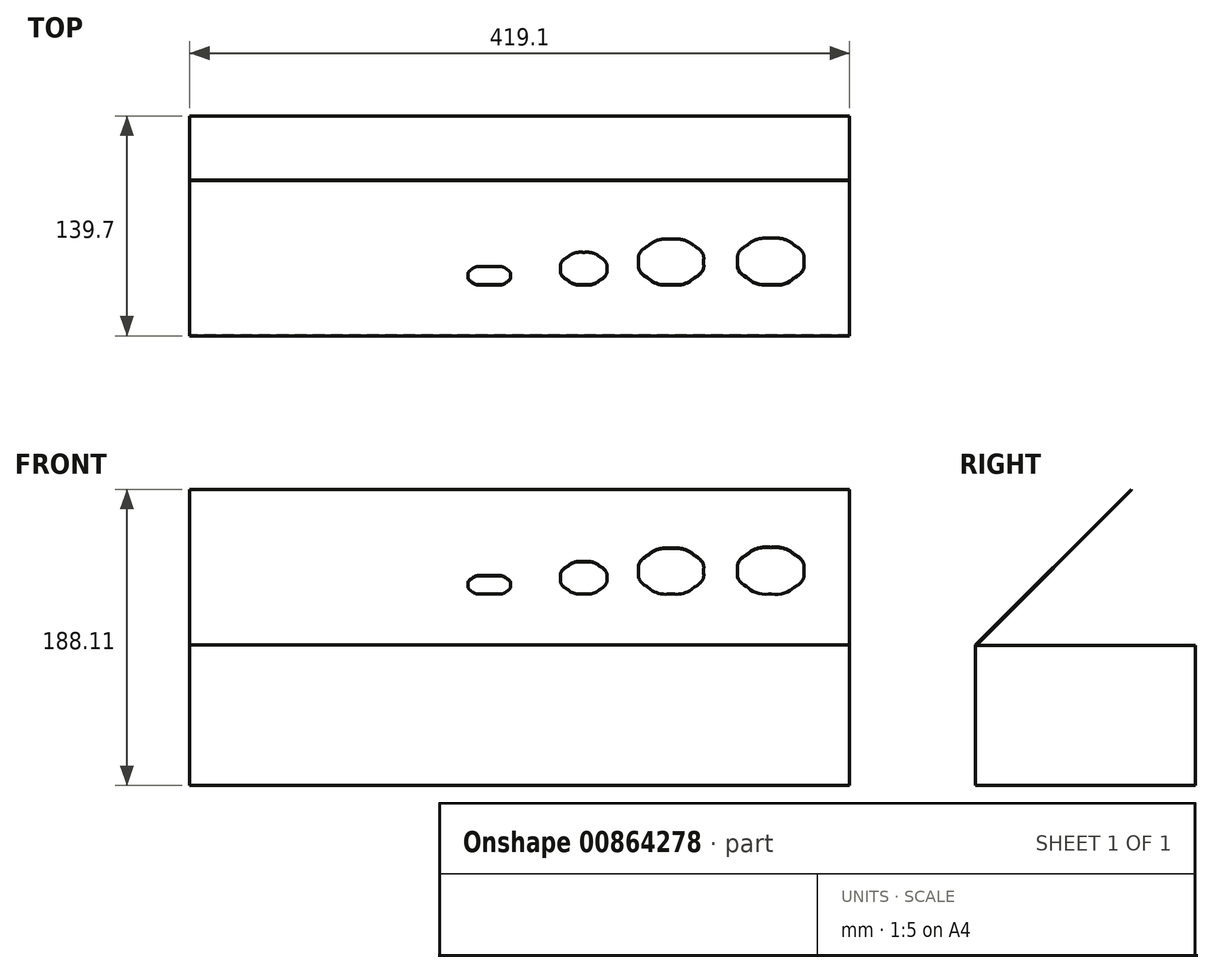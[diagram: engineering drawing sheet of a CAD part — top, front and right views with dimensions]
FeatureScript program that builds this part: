
annotation { "Feature Type Name" : "Feature", "Feature Type Description" : "" }
export const myFeature = defineFeature(function(context is Context, id is Id, definition is map)
    precondition{}
    {
        {
            var Q0;
            Q0=qCreatedBy(makeId("Right.planeOp"),FACE);
            var sketch = newSketch(context, id + "F0", { "sketchPlane" : qUnion([Q0])});
            skLineSegment(sketch, "E0.bottom", {"start": v(0, 0) * mm, "end": v(-139.7, 0) * mm});
            skLineSegment(sketch, "E0.top", {"start": v(0, 88.9) * mm, "end": v(-139.3, 88.9) * mm});
            skLineSegment(sketch, "E0.left", {"start": v(0, 0) * mm, "end": v(0, 88.9) * mm});
            skLineSegment(sketch, "E0.right", {"start": v(-139.7, 0) * mm, "end": v(-139.7, 89.32) * mm});
            skLineSegment(sketch, "E1", {"start": v(-139.7, 89.32) * mm, "end": v(-40.92, 188.1) * mm});
            skLineSegment(sketch, "E2", {"start": v(-40.92, 188.1) * mm, "end": v(-40.63, 187.82) * mm});
            skLineSegment(sketch, "E3", {"start": v(-40.63, 187.82) * mm, "end": v(-139.3, 89.15) * mm});
            skLineSegment(sketch, "E4", {"start": v(-139.3, 88.9) * mm, "end": v(-139.3, 89.15) * mm});
            skLineSegment(sketch, "E5", {"start": v(-139.3, 88.9) * mm, "end": v(-139.7, 88.9) * mm, "construction": true});
            skSolve(sketch);
        }
        {
            var Q0;
            Q0=qSketchRegion(id+"F0",true);
            extrude(context, id + "F1", {"entities" : qUnion([Q0]), "endBound" : BoundingType.SYMMETRIC, "depth" : 419.1 * mm, "offsetDistance" : 25.4 * mm});
        }
        {
            var Q0;
            Q0=makeQuery(id+"F1.opExtrude","SWEPT_FACE",FACE,{"disambiguationData":[OSD([sQuery(id+"F0.wireOp",EDGE,"E1")])]});
            var sketch = newSketch(context, id + "F2", { "sketchPlane" : qUnion([Q0])});
            skLineSegment(sketch, "E6", {"start": v(-24.54, 10.03) * mm, "end": v(-14.22, 10.03) * mm});
            skLineSegment(sketch, "E7", {"start": v(-24.54, 26.7) * mm, "end": v(-14.22, 26.7) * mm});
            skLineSegment(sketch, "E8", {"start": v(-209.88, -34.42) * mm, "end": v(-209.88, 104.5) * mm, "construction": true});
            skLineSegment(sketch, "E9", {"start": v(209.22, -34.42) * mm, "end": v(209.22, 104.5) * mm, "construction": true});
            skLineSegment(sketch, "E10", {"start": v(209.22, -34.42) * mm, "end": v(-209.88, -34.42) * mm, "construction": true});
            skLineSegment(sketch, "E11", {"start": v(-209.88, 104.5) * mm, "end": v(209.22, 104.5) * mm, "construction": true});
            skFitSpline(sketch, "E12", {"points": [v(-24.54, 26.7) * mm, v(-26.72, 26.7) * mm, v(-28.9, 25.8) * mm, v(-30.43, 24.26) * mm]});
            skFitSpline(sketch, "E13", {"points": [v(-30.43, 24.26) * mm, v(-31.98, 22.72) * mm, v(-32.88, 20.55) * mm, v(-32.88, 18.37) * mm, v(-32.88, 16.19) * mm, v(-31.98, 14.02) * mm, v(-30.43, 12.48) * mm]});
            skFitSpline(sketch, "E14", {"points": [v(-30.43, 12.48) * mm, v(-28.9, 10.93) * mm, v(-26.72, 10.03) * mm, v(-24.54, 10.03) * mm]});
            skFitSpline(sketch, "E15", {"points": [v(-14.22, 10.03) * mm, v(-12.04, 10.03) * mm, v(-9.87, 10.93) * mm, v(-8.33, 12.48) * mm]});
            skFitSpline(sketch, "E16", {"points": [v(-8.33, 12.48) * mm, v(-6.79, 14.02) * mm, v(-5.89, 16.19) * mm, v(-5.89, 18.37) * mm, v(-5.89, 20.55) * mm, v(-6.79, 22.72) * mm, v(-8.33, 24.26) * mm]});
            skFitSpline(sketch, "E17", {"points": [v(-8.33, 24.26) * mm, v(-9.87, 25.8) * mm, v(-12.04, 26.7) * mm, v(-14.22, 26.7) * mm]});
            skFitSpline(sketch, "E18", {"points": [v(40.6, 39.4) * mm, v(36.75, 39.4) * mm, v(32.93, 37.82) * mm, v(30.2, 35.1) * mm]});
            skFitSpline(sketch, "E19", {"points": [v(30.2, 35.1) * mm, v(27.49, 32.38) * mm, v(25.9, 28.56) * mm, v(25.9, 24.72) * mm, v(25.9, 20.87) * mm, v(27.49, 17.05) * mm, v(30.2, 14.34) * mm]});
            skFitSpline(sketch, "E20", {"points": [v(30.2, 14.34) * mm, v(32.93, 11.62) * mm, v(36.75, 10.03) * mm, v(40.6, 10.03) * mm, v(44.43, 10.03) * mm, v(48.26, 11.62) * mm, v(50.97, 14.34) * mm]});
            skFitSpline(sketch, "E21", {"points": [v(50.97, 14.34) * mm, v(53.7, 17.05) * mm, v(55.27, 20.87) * mm, v(55.27, 24.72) * mm, v(55.27, 28.56) * mm, v(53.7, 32.38) * mm, v(50.97, 35.1) * mm]});
            skFitSpline(sketch, "E22", {"points": [v(50.97, 35.1) * mm, v(48.26, 37.82) * mm, v(44.43, 39.4) * mm, v(40.6, 39.4) * mm]});
            skFitSpline(sketch, "E23", {"points": [v(96.1, 51.3) * mm, v(90.7, 51.3) * mm, v(85.34, 49.09) * mm, v(81.52, 45.26) * mm]});
            skFitSpline(sketch, "E24", {"points": [v(81.52, 45.26) * mm, v(77.7, 41.44) * mm, v(75.47, 36.07) * mm, v(75.47, 30.67) * mm, v(75.47, 25.27) * mm, v(77.7, 19.9) * mm, v(81.52, 16.08) * mm]});
            skFitSpline(sketch, "E25", {"points": [v(81.52, 16.08) * mm, v(85.34, 12.26) * mm, v(90.7, 10.03) * mm, v(96.1, 10.03) * mm, v(101.51, 10.03) * mm, v(106.88, 12.26) * mm, v(110.7, 16.08) * mm]});
            skFitSpline(sketch, "E26", {"points": [v(110.7, 16.08) * mm, v(114.52, 19.9) * mm, v(116.75, 25.27) * mm, v(116.75, 30.67) * mm, v(116.75, 36.07) * mm, v(114.52, 41.44) * mm, v(110.7, 45.26) * mm]});
            skFitSpline(sketch, "E27", {"points": [v(110.7, 45.26) * mm, v(106.88, 49.09) * mm, v(101.51, 51.3) * mm, v(96.1, 51.3) * mm]});
            skFitSpline(sketch, "E28", {"points": [v(159.43, 52.1) * mm, v(153.93, 52.1) * mm, v(148.45, 49.84) * mm, v(144.56, 45.94) * mm]});
            skFitSpline(sketch, "E29", {"points": [v(144.56, 45.94) * mm, v(140.66, 42.05) * mm, v(138.4, 36.58) * mm, v(138.4, 31.07) * mm, v(138.4, 25.56) * mm, v(140.66, 20.09) * mm, v(144.56, 16.2) * mm, v(148.45, 12.3) * mm, v(153.93, 10.03) * mm, v(159.43, 10.03) * mm, v(164.94, 10.03) * mm, v(170.41, 12.3) * mm, v(174.3, 16.2) * mm]});
            skFitSpline(sketch, "E30", {"points": [v(174.3, 16.2) * mm, v(178.2, 20.09) * mm, v(180.47, 25.56) * mm, v(180.47, 31.07) * mm, v(180.47, 36.58) * mm, v(178.2, 42.05) * mm, v(174.3, 45.94) * mm]});
            skFitSpline(sketch, "E31", {"points": [v(174.3, 45.94) * mm, v(170.41, 49.84) * mm, v(164.94, 52.1) * mm, v(159.43, 52.1) * mm]});
            skSolve(sketch);
        }
        {
            var Q0;
            Q0=qSketchRegion(id+"F2",true);
            var Q1;
            Q1=makeQuery(id+"F1.opExtrude","SWEPT_FACE",FACE,{"disambiguationData":[OSD([sQuery(id+"F0.wireOp",EDGE,"E3")])]});
            extrude(context, id + "F3", {"entities" : qUnion([Q0]), "operationType" : NewBodyOperationType.REMOVE, "endBound" : BoundingType.UP_TO_SURFACE, "oppositeDirection" : true, "depth" : 25.4 * mm, "endBoundEntityFace" : qUnion([Q1]), "offsetDistance" : 25.4 * mm});
        }
    });
